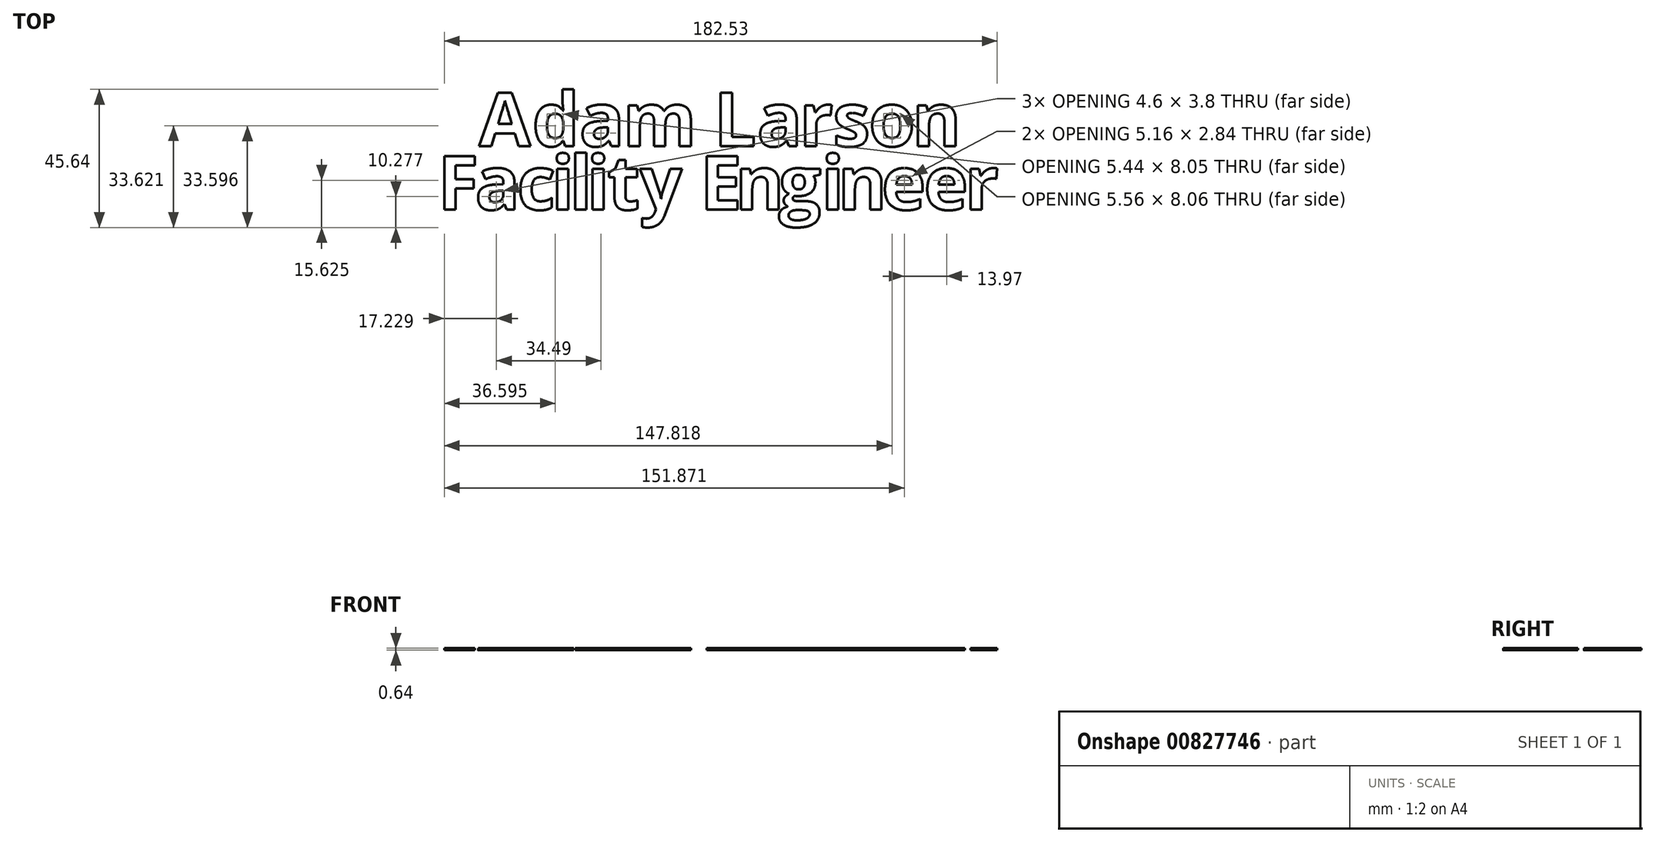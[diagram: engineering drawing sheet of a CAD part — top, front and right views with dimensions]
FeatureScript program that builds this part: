
annotation { "Feature Type Name" : "Feature", "Feature Type Description" : "" }
export const myFeature = defineFeature(function(context is Context, id is Id, definition is map)
    precondition{}
    {
        {
            var Q0;
            Q0=qCreatedBy(makeId("Top.planeOp"),FACE);
            var sketch = newSketch(context, id + "F0", { "sketchPlane" : qUnion([Q0])});
            skText(sketch, "E0", { "text": "A", "fontName": "OpenSans-Bold.ttf"});
            skText(sketch, "E1", { "text": "d", "fontName": "OpenSans-Bold.ttf"});
            skText(sketch, "E2", { "text": "a", "fontName": "OpenSans-Bold.ttf"});
            skText(sketch, "E3", { "text": "m", "fontName": "OpenSans-Bold.ttf"});
            skText(sketch, "E4", { "text": "L", "fontName": "OpenSans-Bold.ttf"});
            skText(sketch, "E5", { "text": "a", "fontName": "OpenSans-Bold.ttf"});
            skText(sketch, "E6", { "text": "r", "fontName": "OpenSans-Bold.ttf"});
            skText(sketch, "E7", { "text": "s", "fontName": "OpenSans-Bold.ttf"});
            skText(sketch, "E8", { "text": "o", "fontName": "OpenSans-Bold.ttf"});
            skText(sketch, "E9", { "text": "F", "fontName": "OpenSans-Bold.ttf"});
            skText(sketch, "E10", { "text": "a", "fontName": "OpenSans-Bold.ttf"});
            skText(sketch, "E11", { "text": "c", "fontName": "OpenSans-Bold.ttf"});
            skText(sketch, "E12", { "text": "i", "fontName": "OpenSans-Bold.ttf"});
            skText(sketch, "E13", { "text": "l", "fontName": "OpenSans-Bold.ttf"});
            skText(sketch, "E14", { "text": "i", "fontName": "OpenSans-Bold.ttf"});
            skText(sketch, "E15", { "text": "t", "fontName": "OpenSans-Bold.ttf"});
            skText(sketch, "E16", { "text": "y", "fontName": "OpenSans-Bold.ttf"});
            skLineSegment(sketch, "E17", {"start": v(-97.85, -29.75) * mm, "end": v(-24.68, -29.75) * mm});
            skLineSegment(sketch, "E18", {"start": v(-3.63, -75.47) * mm, "end": v(-98.68, -75.47) * mm});
            skText(sketch, "E19", { "text": "n", "fontName": "OpenSans-Bold.ttf"});
            skText(sketch, "E20", { "text": "E", "fontName": "OpenSans-Bold.ttf"});
            skText(sketch, "E21", { "text": "n", "fontName": "OpenSans-Bold.ttf"});
            skText(sketch, "E22", { "text": "g", "fontName": "OpenSans-Bold.ttf"});
            skText(sketch, "E23", { "text": "i", "fontName": "OpenSans-Bold.ttf"});
            skText(sketch, "E24", { "text": "n", "fontName": "OpenSans-Bold.ttf"});
            skText(sketch, "E25", { "text": "e", "fontName": "OpenSans-Bold.ttf"});
            skText(sketch, "E26", { "text": "e", "fontName": "OpenSans-Bold.ttf"});
            skText(sketch, "E27", { "text": "r", "fontName": "OpenSans-Bold.ttf"});
            const initialGuessF0  = {"E0": [-0.06287, -0.04855, 1, 0, 0.01778], "E1": [-0.04533, -0.04855, 1, 0, 0.01778], "E2": [-0.02976, -0.04855, 1, 0, 0.01778], "E3": [-0.01539, -0.04855, 1, 0, 0.01778], "E4": [0.01466, -0.04855, 1, 0, 0.01778], "E5": [0.0289, -0.04855, 1, 0, 0.01778], "E6": [0.0428, -0.04855, 1, 0, 0.01778], "E7": [0.0539, -0.04855, 1, 0, 0.01778], "E8": [0.06581, -0.04855, 1, 0, 0.01778], "E9": [-0.07659, -0.0695, 1, 0, 0.01778], "E10": [-0.06425, -0.0695, 1, 0, 0.01778], "E11": [-0.05035, -0.0695, 1, 0, 0.01778], "E12": [-0.03902, -0.0695, 1, 0, 0.01778], "E13": [-0.0331, -0.0695, 1, 0, 0.01778], "E14": [-0.02734, -0.0695, 1, 0, 0.01778], "E15": [-0.02052, -0.0695, 1, 0, 0.01778], "E16": [-0.00988, -0.0695, 1, 0, 0.01778], "E19": [0.08007, -0.04855, 1, 0, 0.01778], "E20": [0.01, -0.0695, 1, 0, 0.01778], "E21": [0.0217, -0.0695, 1, 0, 0.01778], "E22": [0.03603, -0.0695, 1, 0, 0.01778], "E23": [0.05013, -0.0695, 1, 0, 0.01778], "E24": [0.05561, -0.0695, 1, 0, 0.01778], "E25": [0.07, -0.0695, 1, 0, 0.01778], "E26": [0.08397, -0.0695, 1, 0, 0.01778], "E27": [0.09746, -0.0695, 1, 0, 0.01778]};
            skSetInitialGuess(sketch, initialGuessF0);
            skSolve(sketch);
        }
        {
            var Q0;
            Q0 = qSketchRegion(id + "F0", true);
            extrude(context, id + "F1", {"entities" : qUnion([Q0]), "depth" : 0.64 * mm, "offsetDistance" : 25.4 * mm});
        }
    });
